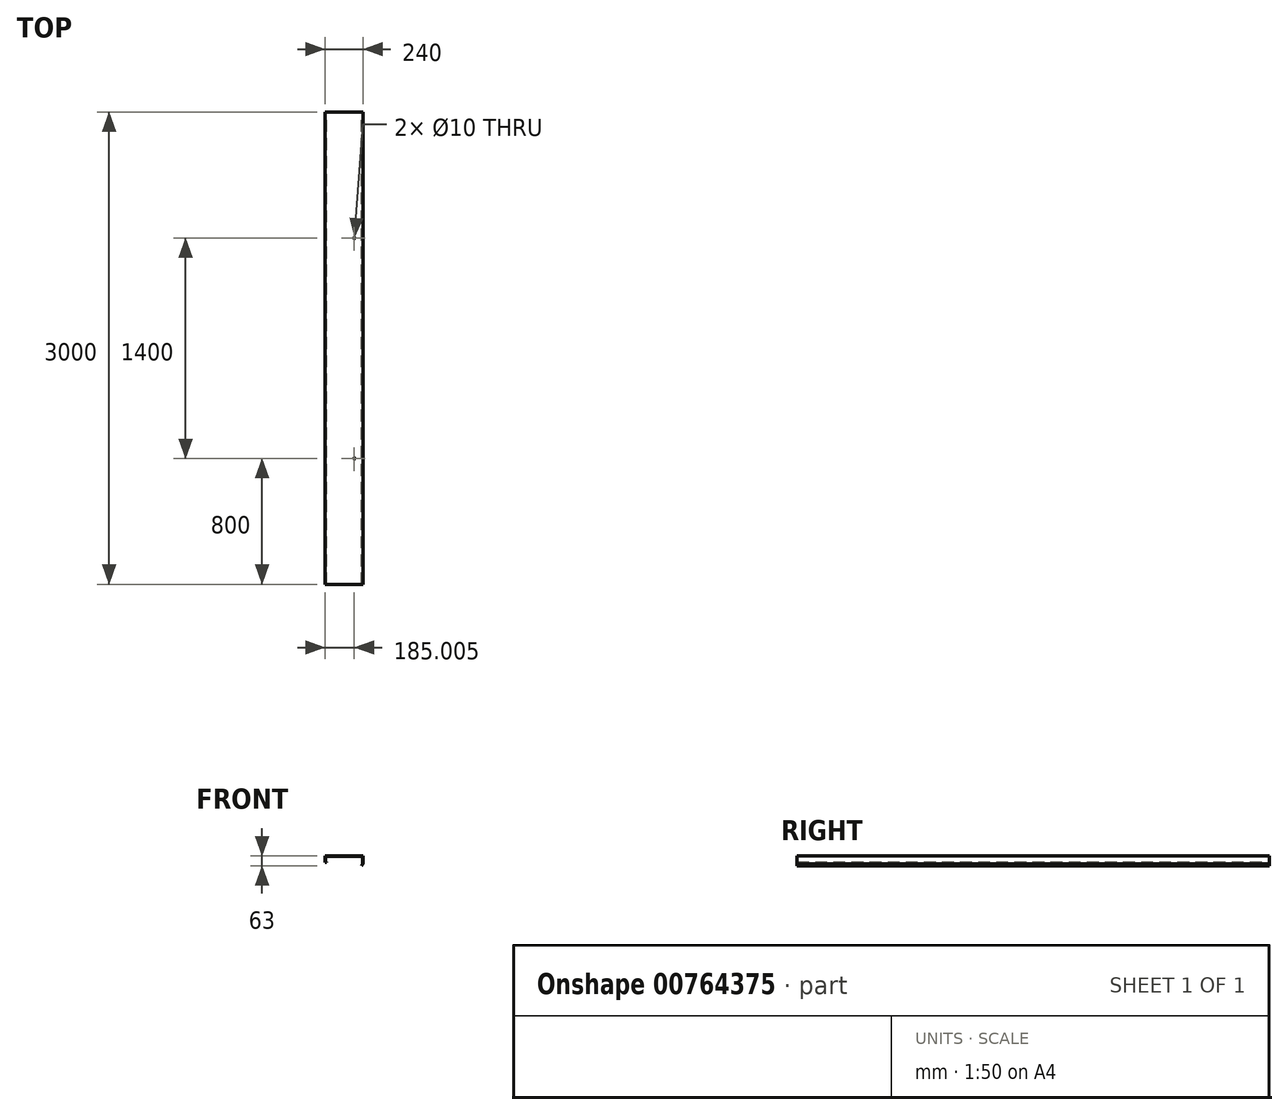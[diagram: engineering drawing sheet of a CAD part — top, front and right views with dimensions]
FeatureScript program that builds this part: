
annotation { "Feature Type Name" : "Feature", "Feature Type Description" : "" }
export const myFeature = defineFeature(function(context is Context, id is Id, definition is map)
    precondition{}
    {
        {
            var Q0;
            Q0=qCreatedBy(makeId("Front.planeOp"),FACE);
            var sketch = newSketch(context, id + "F0", { "sketchPlane" : qUnion([Q0])});
            skLineSegment(sketch, "E0", {"start": v(-82.78, 2) * mm, "end": v(117.22, 2) * mm});
            skLineSegment(sketch, "E1", {"start": v(117.22, 2) * mm, "end": v(117.22, -48) * mm});
            skLineSegment(sketch, "E2", {"start": v(117.22, -48) * mm, "end": v(109.74, -61) * mm});
            skLineSegment(sketch, "E3.0", {"start": v(115.22, -47.47) * mm, "end": v(108, -60) * mm});
            skLineSegment(sketch, "E3.1", {"start": v(115.22, 0) * mm, "end": v(115.22, -47.47) * mm});
            skLineSegment(sketch, "E3.2", {"start": v(-82.78, 0) * mm, "end": v(115.22, 0) * mm});
            skLineSegment(sketch, "E4", {"start": v(109.74, -61) * mm, "end": v(108, -60) * mm});
            skLineSegment(sketch, "E5", {"start": v(-82.78, 2) * mm, "end": v(-122.78, 2) * mm});
            skLineSegment(sketch, "E6", {"start": v(-122.78, 2) * mm, "end": v(-122.78, -38) * mm});
            skLineSegment(sketch, "E7", {"start": v(-122.78, -38) * mm, "end": v(-112.78, -38) * mm});
            skLineSegment(sketch, "E8.0", {"start": v(-120.78, -36) * mm, "end": v(-112.78, -36) * mm});
            skLineSegment(sketch, "E8.1", {"start": v(-120.78, 0) * mm, "end": v(-120.78, -36) * mm});
            skLineSegment(sketch, "E8.2", {"start": v(-82.78, 0) * mm, "end": v(-120.78, 0) * mm});
            skLineSegment(sketch, "E9", {"start": v(-112.78, -38) * mm, "end": v(-112.78, -36) * mm});
            skSolve(sketch);
        }
        {
            var Q0;
            Q0=makeQuery(id+"F0.imprint","IMPRINT",FACE,{"disambiguationData":[TD([[makeQuery(id+"F0.imprint","IMPRINT",EDGE,{"derivedFrom":sQuery(id+"F0.wireOp",EDGE,"E0")}),-1.0]])]});
            extrude(context, id + "F1", {"entities" : qUnion([Q0]), "depth" : 3000 * mm, "offsetDistance" : 25 * mm, "symmetric" : true});
        }
        {
            var Q0;
            Q0=makeQuery(id+"F1.opExtrude","SWEPT_FACE",FACE,{"disambiguationData":[OSD([sQuery(id+"F0.wireOp",EDGE,"E0")])]});
            var sketch = newSketch(context, id + "F2", { "sketchPlane" : qUnion([Q0])});
            skCircle(sketch, "E10", {"center": v(62.22, -700) * mm, "radius": 3.5 * mm});
            skCircle(sketch, "E11", {"center": v(62.22, 700) * mm, "radius": 5 * mm});
            skSolve(sketch);
        }
        {
            var Q0;
            Q0=sQuery(id+"F2.wireOp",VERTEX,"E10.center");
            var Q1;
            Q1=sQuery(id+"F2.wireOp",VERTEX,"E11.center");
            var Q2;
            Q2=makeQuery(id+"F1.opExtrude","SWEPT_BODY",BODY,{"disambiguationData":[OSD([sQuery(id+"F0.wireOp",EDGE,"E0"),sQuery(id+"F0.wireOp",EDGE,"E1"),sQuery(id+"F0.wireOp",EDGE,"E2"),sQuery(id+"F0.wireOp",EDGE,"E3.0"),sQuery(id+"F0.wireOp",EDGE,"E3.1"),sQuery(id+"F0.wireOp",EDGE,"E3.2"),sQuery(id+"F0.wireOp",EDGE,"NZ3Mv3ZF-DXOj-N4za-GzoJ-AIFyZdtJidZr"),sQuery(id+"F0.wireOp",EDGE,"E4")])]});
            hole(context, id + "F3", {"style" : HoleStyle.SIMPLE, "endStyle" : HoleEndStyle.THROUGH, "holeDiameter" : 10 * mm, "majorDiameter" : 5 * mm, "isTappedThrough" : true, "tappedDepth" : 12 * mm, "tapClearance" : 3, "locations" : qUnion([Q0, Q1]), "scope" : qUnion([Q2]), "startStyle" : HoleStartStyle.PART});
        }
    });
